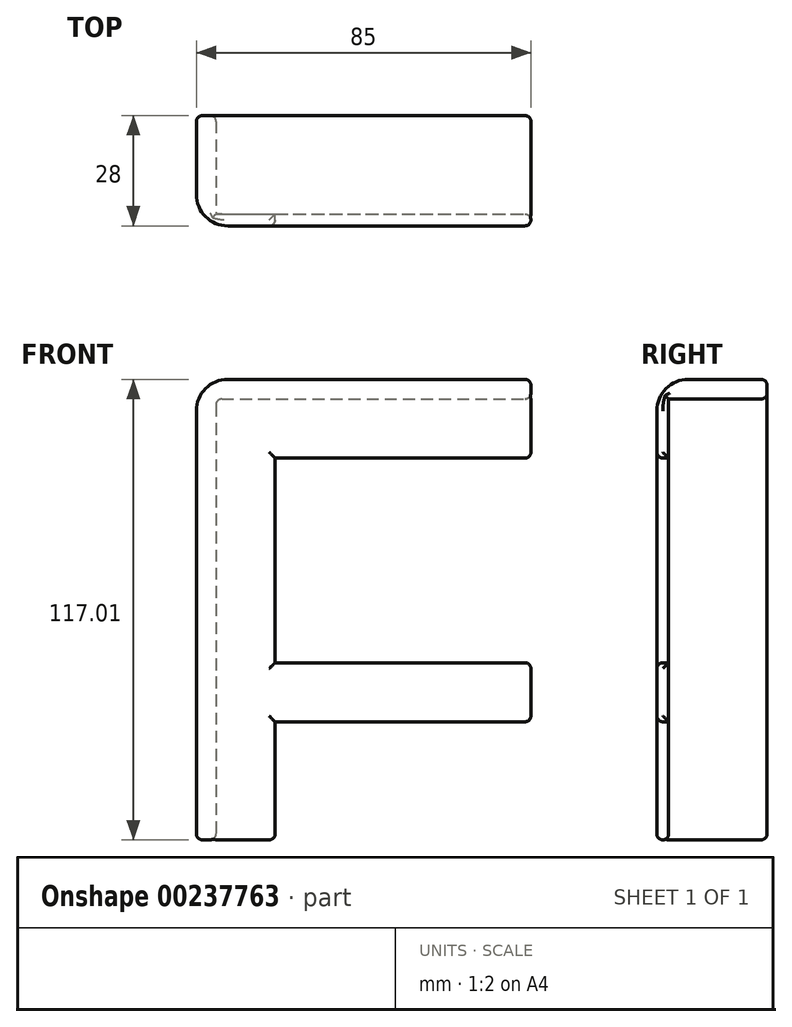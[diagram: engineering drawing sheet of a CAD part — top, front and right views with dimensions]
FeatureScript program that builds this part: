
annotation { "Feature Type Name" : "Feature", "Feature Type Description" : "" }
export const myFeature = defineFeature(function(context is Context, id is Id, definition is map)
    precondition{}
    {
        {
            var Q0;
            Q0=qCreatedBy(makeId("Front.planeOp"),FACE);
            var sketch = newSketch(context, id + "F0", { "sketchPlane" : qUnion([Q0])});
            skLineSegment(sketch, "E0.bottom", {"start": v(-83.34, 95.73) * mm, "end": v(1.66, 95.73) * mm});
            skLineSegment(sketch, "E0.top", {"start": v(-83.34, -21.27) * mm, "end": v(1.66, -21.27) * mm});
            skLineSegment(sketch, "E0.left", {"start": v(-83.34, 95.73) * mm, "end": v(-83.34, -21.27) * mm});
            skLineSegment(sketch, "E0.right", {"start": v(1.66, 95.73) * mm, "end": v(1.66, -21.27) * mm});
            skLineSegment(sketch, "E1.bottom", {"start": v(-78.34, 90.73) * mm, "end": v(1.66, 90.73) * mm});
            skLineSegment(sketch, "E1.top", {"start": v(-78.34, -21.27) * mm, "end": v(1.66, -21.27) * mm});
            skLineSegment(sketch, "E1.left", {"start": v(-78.34, 90.73) * mm, "end": v(-78.34, -21.27) * mm});
            skLineSegment(sketch, "E1.right", {"start": v(1.66, 90.73) * mm, "end": v(1.66, -21.27) * mm});
            skLineSegment(sketch, "E2.bottom", {"start": v(-63.34, 75.73) * mm, "end": v(1.66, 75.73) * mm});
            skLineSegment(sketch, "E2.top", {"start": v(-63.34, 23.73) * mm, "end": v(1.66, 23.73) * mm});
            skLineSegment(sketch, "E2.left", {"start": v(-63.34, 75.73) * mm, "end": v(-63.34, 23.73) * mm});
            skLineSegment(sketch, "E2.right", {"start": v(1.66, 75.73) * mm, "end": v(1.66, 23.73) * mm});
            skLineSegment(sketch, "E3.bottom", {"start": v(-63.34, 8.73) * mm, "end": v(1.66, 8.73) * mm});
            skLineSegment(sketch, "E3.top", {"start": v(-63.34, -21.27) * mm, "end": v(1.66, -21.27) * mm});
            skLineSegment(sketch, "E3.left", {"start": v(-63.34, 8.73) * mm, "end": v(-63.34, -21.27) * mm});
            skLineSegment(sketch, "E3.right", {"start": v(1.66, 8.73) * mm, "end": v(1.66, -21.27) * mm});
            skSolve(sketch);
        }
        {
            var Q0;
            {var subQ0=sQuery(id+"F0.wireOp",EDGE,"E1.bottom");Q0=makeQuery(id+"F0.imprint","IMPRINT",FACE,{"disambiguationData":[TD([[makeQuery(id+"F0.imprint","IMPRINT",EDGE,{"derivedFrom":subQ0}),-1.0]])]});}
            var Q1;
            {var subQ1=sQuery(id+"F0.wireOp",EDGE,"E0.bottom");Q1=makeQuery(id+"F0.imprint","IMPRINT",FACE,{"disambiguationData":[TD([[makeQuery(id+"F0.imprint","IMPRINT",EDGE,{"derivedFrom":subQ1}),-1.0]])]});}
            extrude(context, id + "F1", {"entities" : qUnion([Q0, Q1]), "depth" : 3 * mm, "offsetDistance" : 25 * mm});
        }
        {
            var Q0;
            {var subQ1=sQuery(id+"F0.wireOp",EDGE,"E0.bottom");Q0=makeQuery(id+"F0.imprint","IMPRINT",FACE,{"disambiguationData":[TD([[makeQuery(id+"F0.imprint","IMPRINT",EDGE,{"derivedFrom":subQ1}),-1.0]])]});}
            extrude(context, id + "F2", {"entities" : qUnion([Q0]), "operationType" : NewBodyOperationType.ADD, "oppositeDirection" : true, "depth" : 25 * mm, "offsetDistance" : 25 * mm});
        }
        {
            var Q0;
            {var subQ0=sQuery(id+"F0.wireOp",EDGE,"E0.left");var subQ1=sQuery(id+"F0.wireOp",EDGE,"E0.bottom");Q0=makeQuery(id+"F2.boolean.opBoolean","MERGE",EDGE,{"derivedFrom":[makeQuery(id+"F1.opExtrude","SWEPT_EDGE",EDGE,{"disambiguationData":[OSD([subQ1,subQ0])]}),makeQuery(id+"F2.opExtrude","SWEPT_EDGE",EDGE,{"disambiguationData":[OSD([subQ1,subQ0])]})]});}
            var Q1;
            Q1=makeQuery(id+"F1.opExtrude","CAP_EDGE",EDGE,{"disambiguationData":[OSD([sQuery(id+"F0.wireOp",EDGE,"E0.bottom")])],"isStart":false});
            var Q2;
            Q2=makeQuery(id+"F1.opExtrude","CAP_EDGE",EDGE,{"disambiguationData":[OSD([sQuery(id+"F0.wireOp",EDGE,"E0.left")])],"isStart":false});
            fillet(context, id + "F3", {"entities" : qUnion([Q0, Q1, Q2]), "tangentPropagation" : true, "radius" : 8 * mm, "defaultsChanged" : false, "vertexSettings" : [], "allowEdgeOverflow" : false});
        }
        {
            var Q0;
            Q0=makeQuery(id+"F2.opExtrude","CAP_FACE",FACE,{"disambiguationData":[OSD([sQuery(id+"F0.wireOp",EDGE,"E0.bottom"),sQuery(id+"F0.wireOp",EDGE,"E0.top"),sQuery(id+"F0.wireOp",EDGE,"E0.left"),sQuery(id+"F0.wireOp",EDGE,"E0.right"),sQuery(id+"F0.wireOp",EDGE,"E1.bottom"),sQuery(id+"F0.wireOp",EDGE,"E1.left")])],"isStart":false});
            var Q1;
            {var subQ0=sQuery(id+"F0.wireOp",EDGE,"E0.right");Q1=makeQuery(id+"F2.boolean.opBoolean","MERGE",FACE,{"derivedFrom":[makeQuery(id+"F1.opExtrude","SWEPT_FACE",FACE,{"disambiguationData":[OSD([subQ0]),TDD([makeQuery(id+"F0.imprint","IMPRINT",EDGE,{"disambiguationData":[TD([[makeQuery(id+"F0.imprint","INTERSECT",VERTEX,{"derivedFrom":[subQ0,sQuery(id+"F0.wireOp",EDGE,"E2.bottom")]}),1.0]])],"derivedFrom":subQ0}),makeQuery(id+"F0.imprint","IMPRINT",EDGE,{"disambiguationData":[TD([[makeQuery(id+"F0.imprint","INTERSECT",VERTEX,{"derivedFrom":[sQuery(id+"F0.wireOp",EDGE,"E0.bottom"),subQ0]}),-1.0]])],"derivedFrom":subQ0})])]}),makeQuery(id+"F2.opExtrude","SWEPT_FACE",FACE,{"disambiguationData":[OSD([subQ0])]})]});}
            var Q2;
            {var subQ0=sQuery(id+"F0.wireOp",EDGE,"E0.right");Q2=makeQuery(id+"F1.opExtrude","SWEPT_FACE",FACE,{"disambiguationData":[OSD([subQ0]),TDD([makeQuery(id+"F0.imprint","IMPRINT",EDGE,{"disambiguationData":[TD([[makeQuery(id+"F0.imprint","INTERSECT",VERTEX,{"derivedFrom":[subQ0,sQuery(id+"F0.wireOp",EDGE,"E2.top")]}),-1.0]])],"derivedFrom":subQ0})])]});}
            var Q3;
            Q3=makeQuery(id+"F1.opExtrude","CAP_EDGE",EDGE,{"disambiguationData":[OSD([sQuery(id+"F0.wireOp",EDGE,"E2.bottom")])],"isStart":false});
            var Q4;
            Q4=makeQuery(id+"F1.opExtrude","CAP_EDGE",EDGE,{"disambiguationData":[OSD([sQuery(id+"F0.wireOp",EDGE,"E2.left")])],"isStart":false});
            var Q5;
            Q5=makeQuery(id+"F1.opExtrude","CAP_EDGE",EDGE,{"disambiguationData":[OSD([sQuery(id+"F0.wireOp",EDGE,"E3.left")])],"isStart":false});
            var Q6;
            Q6=makeQuery(id+"F1.opExtrude","CAP_EDGE",EDGE,{"disambiguationData":[OSD([sQuery(id+"F0.wireOp",EDGE,"E2.top")])],"isStart":false});
            var Q7;
            Q7=makeQuery(id+"F1.opExtrude","CAP_EDGE",EDGE,{"disambiguationData":[OSD([sQuery(id+"F0.wireOp",EDGE,"E3.bottom")])],"isStart":false});
            var Q8;
            {var subQ0=sQuery(id+"F0.wireOp",EDGE,"E0.top");Q8=makeQuery(id+"F2.boolean.opBoolean","MERGE",FACE,{"derivedFrom":[makeQuery(id+"F1.opExtrude","SWEPT_FACE",FACE,{"disambiguationData":[OSD([subQ0])]}),makeQuery(id+"F2.opExtrude","SWEPT_FACE",FACE,{"disambiguationData":[OSD([subQ0])]})]});}
            var Q9;
            Q9=makeQuery(id+"F2.opExtrude","SWEPT_EDGE",EDGE,{"disambiguationData":[OSD([sQuery(id+"F0.wireOp",EDGE,"E1.bottom"),sQuery(id+"F0.wireOp",EDGE,"E1.left")])]});
            var Q10;
            Q10=makeQuery(id+"F2.opExtrude","CAP_EDGE",EDGE,{"disambiguationData":[OSD([sQuery(id+"F0.wireOp",EDGE,"E1.bottom")])],"isStart":true});
            var Q11;
            Q11=makeQuery(id+"F2.opExtrude","CAP_EDGE",EDGE,{"disambiguationData":[OSD([sQuery(id+"F0.wireOp",EDGE,"E1.left")])],"isStart":true});
            fillet(context, id + "F4", {"entities" : qUnion([Q0, Q1, Q2, Q3, Q4, Q5, Q6, Q7, Q8, Q9, Q10, Q11]), "tangentPropagation" : true, "radius" : 1.5 * mm, "defaultsChanged" : false, "vertexSettings" : [], "allowEdgeOverflow" : false});
        }
    });
